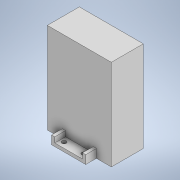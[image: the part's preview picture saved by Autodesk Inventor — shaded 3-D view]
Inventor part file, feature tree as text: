
AUTODESK INVENTOR PART (.ipt)
format: ipt  version: 2021.4 (Build 254397000, 397)  size: 267,776 bytes
history: native  units: mm
features: sketch x4, extrude x3, other x1, hole x1
ambient origin geometry x8: Origin, YZ Plane, XZ Plane, XY Plane, X Axis, Y Axis, Z Axis, Center Point
bodies: Body1 (feature_tree)
feature tree (9):
  other  "ソリッド1"
  extrude  "押し出し1"  Depth=60.0mm
  extrude  "押し出し2"  Depth=30.0mm
  extrude  "押し出し3"  Depth=85.0mm TaperAngle=0.0deg
  hole  "穴1"  [1 undecoded]
  sketch  "スケッチ1"
  sketch  "スケッチ2"
  sketch  "スケッチ3"
  sketch  "スケッチ4"
note: 1 required parameter value undecoded (feature->parameter linkage not recoverable at this tier; creation-order binding heuristic only, values carry confidence <= 0.55)
